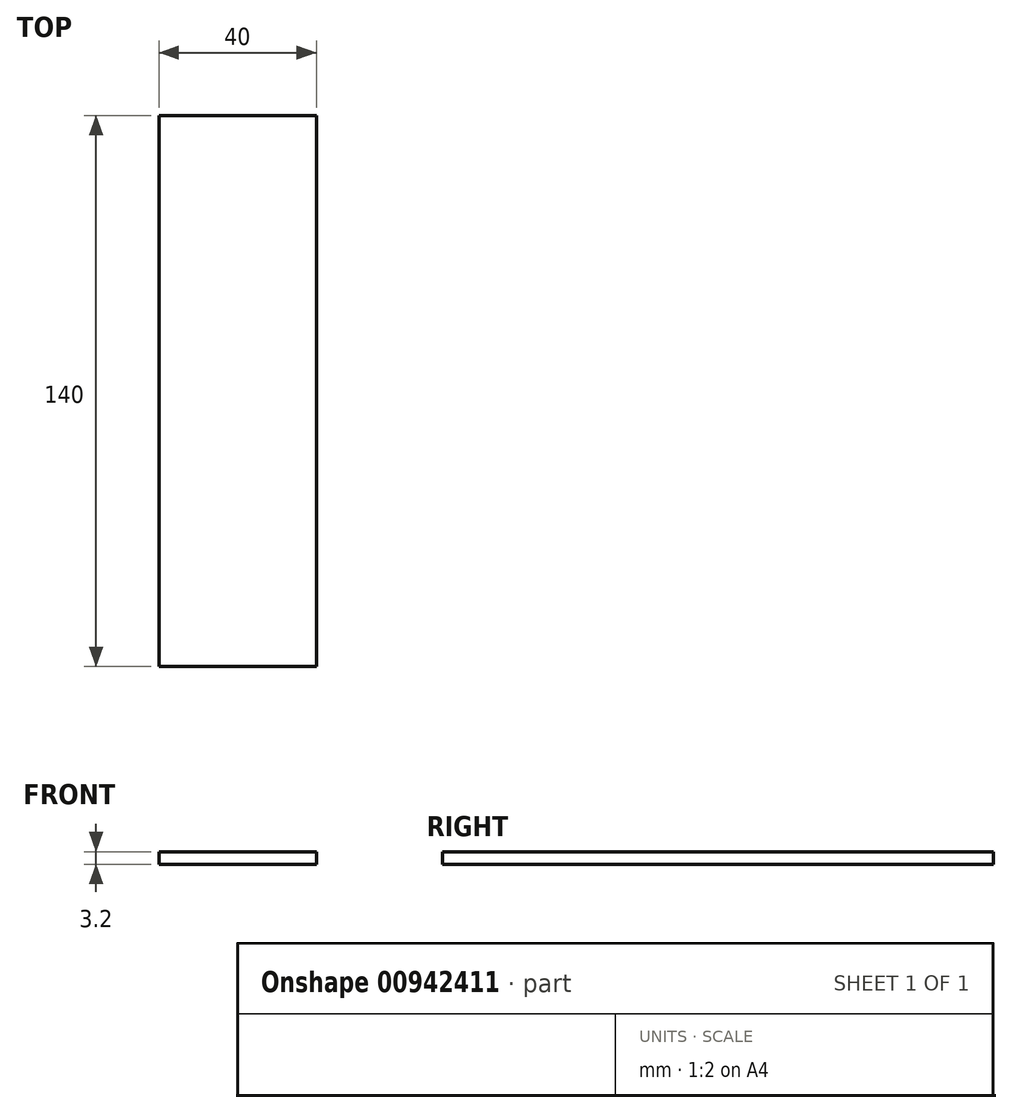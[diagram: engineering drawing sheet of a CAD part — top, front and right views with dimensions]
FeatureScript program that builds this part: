
annotation { "Feature Type Name" : "Feature", "Feature Type Description" : "" }
export const myFeature = defineFeature(function(context is Context, id is Id, definition is map)
    precondition{}
    {
        {
            var Q0;
            Q0=qCreatedBy(makeId("Top.planeOp"),FACE);
            var sketch = newSketch(context, id + "F0", { "sketchPlane" : qUnion([Q0])});
            skLineSegment(sketch, "E0.bottom", {"start": v(0, 0) * mm, "end": v(40, 0) * mm});
            skLineSegment(sketch, "E0.top", {"start": v(0, -140) * mm, "end": v(40, -140) * mm});
            skLineSegment(sketch, "E0.left", {"start": v(0, 0) * mm, "end": v(0, -140) * mm});
            skLineSegment(sketch, "E0.right", {"start": v(40, 0) * mm, "end": v(40, -140) * mm});
            skSolve(sketch);
        }
        {
            var Q0;
            Q0=makeQuery(id+"F0.imprint","IMPRINT",FACE,{"disambiguationData":[TD([[makeQuery(id+"F0.imprint","IMPRINT",EDGE,{"derivedFrom":sQuery(id+"F0.wireOp",EDGE,"E0.bottom")}),-1.0]])]});
            extrude(context, id + "F1", {"entities" : qUnion([Q0]), "depth" : 3.2 * mm, "offsetDistance" : 25 * mm});
        }
    });
